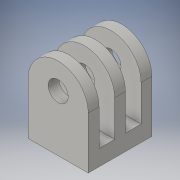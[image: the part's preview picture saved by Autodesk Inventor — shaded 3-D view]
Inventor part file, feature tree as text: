
AUTODESK INVENTOR PART (.ipt)
format: ipt  version: 2016 (Build 200138000, 138)  size: 151,040 bytes
history: native  units: in
note: dims shown in document units (in); Inventor stores cm internally (conversion verified against a paired STEP export)
features: extrude x3, sketch x3, fillet x1
ambient origin geometry x8: Origin, YZ Plane, XZ Plane, XY Plane, X Axis, Y Axis, Z Axis, Center Point
bodies: Solid1 (feature_tree)
feature tree (7):
  extrude  "Extrusion1"  Depth=0.2953in
  fillet  "Fillet1"  Radius=0.6496in
  extrude  "Extrusion8"  Depth=0.2559in
  extrude  "Extrusion9"  Depth=0.2953in
  sketch  "Sketch4"  dims[d0=0.2953in d1=0.2953in d2=0.6496in]
  sketch  "Sketch13"  dims[d3=0.1969in d4=0.2559in]
  sketch  "Sketch14"  dims[d5=0.626in d6=0.0in d7=0.2953in d47=0.1063in d48=0.1063in d49=0.1063in d50=0.626in d51=0.1535in d52=0.1535in d53=1.0in d54=0.0in d55=0.1575in d56=0.0in]
